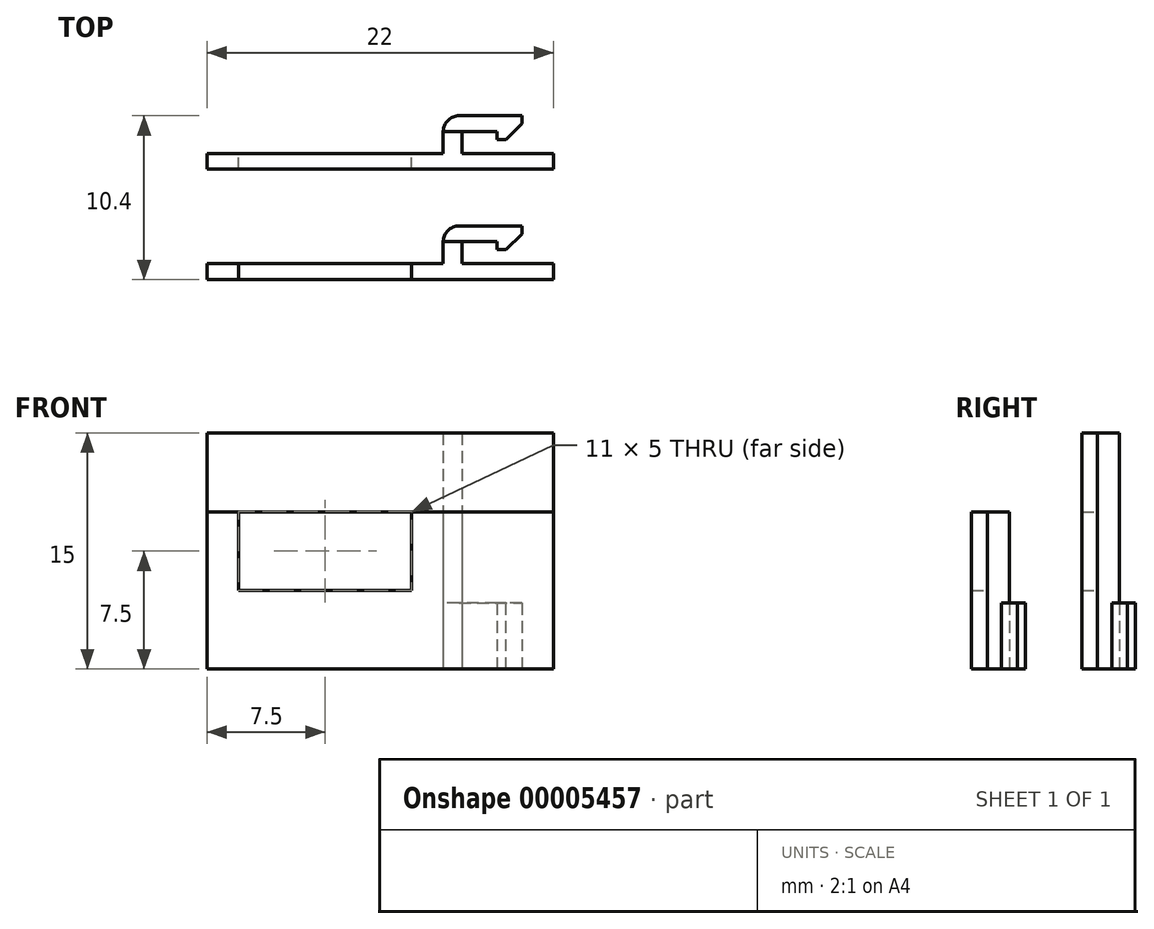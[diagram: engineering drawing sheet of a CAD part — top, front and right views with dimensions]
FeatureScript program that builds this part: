
annotation { "Feature Type Name" : "Feature", "Feature Type Description" : "" }
export const myFeature = defineFeature(function(context is Context, id is Id, definition is map)
    precondition{}
    {
        {
            var Q0;
            Q0=qCreatedBy(makeId("Top.planeOp"),FACE);
            var sketch = newSketch(context, id + "F0", { "sketchPlane" : qUnion([Q0])});
            skLineSegment(sketch, "E0.bottom", {"start": v(7, 0) * mm, "end": v(-15, 0) * mm});
            skLineSegment(sketch, "E0.top", {"start": v(7, -1) * mm, "end": v(-15, -1) * mm});
            skLineSegment(sketch, "E0.left", {"start": v(7, 0) * mm, "end": v(7, -1) * mm});
            skLineSegment(sketch, "E0.right", {"start": v(-15, 0) * mm, "end": v(-15, -1) * mm});
            skLineSegment(sketch, "E1", {"start": v(0, 0) * mm, "end": v(0, 1.4) * mm});
            skLineSegment(sketch, "E2", {"start": v(1, 2.4) * mm, "end": v(5, 2.4) * mm});
            skLineSegment(sketch, "E3", {"start": v(5, 2.4) * mm, "end": v(5, 0.9) * mm});
            skLineSegment(sketch, "E4", {"start": v(5, 0.9) * mm, "end": v(3.4, 0.9) * mm});
            skLineSegment(sketch, "E5", {"start": v(3.4, 0.9) * mm, "end": v(3.4, 1.4) * mm});
            skLineSegment(sketch, "E6", {"start": v(3.4, 1.4) * mm, "end": v(1.2, 1.4) * mm});
            skLineSegment(sketch, "E7", {"start": v(1.2, 1.4) * mm, "end": v(1.2, 0) * mm});
            skPoint(sketch, "E8.visualSharp", {"position": v(3.4, 0.9) * mm});
            skPoint(sketch, "E9.visualSharp", {"position": v(5, 0.9) * mm});
            skPoint(sketch, "E10.visualSharp", {"position": v(5, 2.4) * mm});
            skPoint(sketch, "E11.visualSharp", {"position": v(0, 2.4) * mm});
            skArc(sketch, "E11.filletArc", {"start": v(1, 2.4) * mm, "mid": v(0.3, 2.1) * mm, "end": v(0, 1.4) * mm});
            skLineSegment(sketch, "E12", {"start": v(0, 1.4) * mm, "end": v(1.2, 1.4) * mm});
            skSolve(sketch);
        }
        {
            var Q0;
            Q0=makeQuery(id+"F0.imprint","IMPRINT",FACE,{"disambiguationData":[TD([[makeQuery(id+"F0.imprint","IMPRINT",EDGE,{"derivedFrom":sQuery(id+"F0.wireOp",EDGE,"E2")}),-1.0]])]});
            extrude(context, id + "F1", {"entities" : qUnion([Q0]), "depth" : 4.2 * mm});
        }
        {
            var Q0;
            Q0=makeQuery(id+"F0.imprint","IMPRINT",FACE,{"disambiguationData":[TD([[makeQuery(id+"F0.imprint","IMPRINT",EDGE,{"derivedFrom":sQuery(id+"F0.wireOp",EDGE,"E0.top")}),-1.0]])]});
            var Q1;
            {var subQ1=sQuery(id+"F0.wireOp",EDGE,"E1");Q1=makeQuery(id+"F0.imprint","IMPRINT",FACE,{"disambiguationData":[TD([[makeQuery(id+"F0.imprint","IMPRINT",EDGE,{"derivedFrom":subQ1}),-1.0]])]});}
            extrude(context, id + "F2", {"entities" : qUnion([Q0, Q1]), "operationType" : NewBodyOperationType.ADD, "depth" : 10 * mm});
        }
        {
            var Q0;
            Q0=makeQuery(id+"F1.opExtrude","SWEPT_BODY",BODY,{"disambiguationData":[OSD([sQuery(id+"F0.wireOp",EDGE,"E2"),sQuery(id+"F0.wireOp",EDGE,"E3"),sQuery(id+"F0.wireOp",EDGE,"E4"),sQuery(id+"F0.wireOp",EDGE,"E5"),sQuery(id+"F0.wireOp",EDGE,"E6"),sQuery(id+"F0.wireOp",EDGE,"E8.filletArc"),sQuery(id+"F0.wireOp",EDGE,"E9.filletArc"),sQuery(id+"F0.wireOp",EDGE,"E10.filletArc"),sQuery(id+"F0.wireOp",EDGE,"E11.filletArc"),sQuery(id+"F0.wireOp",EDGE,"E12")])]});
            transform(context, id + "F3", {"entities" : qUnion([Q0]), "transformType" : TransformType.TRANSLATION_3D, "dx" : 0 * mm, "dy" : 7 * mm, "dz" : 0 * mm, "makeCopy" : true});
        }
        {
            var Q0;
            Q0=makeQuery(id+"F3.opPattern","COPY",FACE,{"derivedFrom":makeQuery(id+"F2.opExtrude","CAP_FACE",FACE,{"disambiguationData":[OSD([sQuery(id+"F0.wireOp",EDGE,"E0.bottom"),sQuery(id+"F0.wireOp",EDGE,"E0.top"),sQuery(id+"F0.wireOp",EDGE,"E0.left"),sQuery(id+"F0.wireOp",EDGE,"E0.right"),sQuery(id+"F0.wireOp",EDGE,"E1"),sQuery(id+"F0.wireOp",EDGE,"E7"),sQuery(id+"F0.wireOp",EDGE,"E12")])],"isStart":false}),"instanceName":"1"});
            extrude(context, id + "F4", {"entities" : qUnion([Q0]), "operationType" : NewBodyOperationType.ADD, "offsetDistance" : 25 * mm, "depth" : 5 * mm});
        }
        {
            var Q0;
            Q0=makeQuery(id+"F1.opExtrude","SWEPT_EDGE",EDGE,{"disambiguationData":[OSD([sQuery(id+"F0.wireOp",EDGE,"E3"),sQuery(id+"F0.wireOp",EDGE,"E4")])]});
            var Q1;
            Q1=makeQuery(id+"F3.opPattern","COPY",EDGE,{"derivedFrom":makeQuery(id+"F1.opExtrude","SWEPT_EDGE",EDGE,{"disambiguationData":[OSD([sQuery(id+"F0.wireOp",EDGE,"E3"),sQuery(id+"F0.wireOp",EDGE,"E4")])]}),"instanceName":"1"});
            chamfer(context, id + "F5", {"entities" : qUnion([Q0, Q1]), "width" : 1 * mm, "tangentPropagation" : true});
        }
        {
            var Q0;
            {var subQ0=sQuery(id+"F0.wireOp",EDGE,"E0.bottom");var subQ1=makeQuery(id+"F0.imprint","IMPRINT",EDGE,{"disambiguationData":[TD([[makeQuery(id+"F0.imprint","INTERSECT",VERTEX,{"derivedFrom":[subQ0,sQuery(id+"F0.wireOp",EDGE,"E0.right")]}),1.0]])],"derivedFrom":subQ0});Q0=makeQuery(id+"F4.boolean.opBoolean","MERGE",FACE,{"derivedFrom":[makeQuery(id+"F3.opPattern","COPY",FACE,{"derivedFrom":makeQuery(id+"F2.opExtrude","SWEPT_FACE",FACE,{"disambiguationData":[OSD([subQ0]),TDD([subQ1])]}),"instanceName":"1"}),makeQuery(id+"F4.opExtrude","SWEPT_FACE",FACE,{"disambiguationData":[OSD([subQ0]),TDD([makeQuery(id+"F3.opPattern","COPY",EDGE,{"derivedFrom":makeQuery(id+"F2.opExtrude","CAP_EDGE",EDGE,{"disambiguationData":[OSD([subQ0]),TDD([subQ1])],"isStart":false}),"instanceName":"1"})])]})]});}
            var sketch = newSketch(context, id + "F6", { "sketchPlane" : qUnion([Q0])});
            skLineSegment(sketch, "E13.bottom", {"start": v(13, 5) * mm, "end": v(2, 5) * mm});
            skLineSegment(sketch, "E13.top", {"start": v(13, 10) * mm, "end": v(2, 10) * mm});
            skLineSegment(sketch, "E13.left", {"start": v(13, 5) * mm, "end": v(13, 10) * mm});
            skLineSegment(sketch, "E13.right", {"start": v(2, 5) * mm, "end": v(2, 10) * mm});
            skPoint(sketch, "E13.middle", {"position": v(7.5, 7.5) * mm});
            skPoint(sketch, "E13.middle.positionSnap0", {"position": v(7.5, 15) * mm});
            skPoint(sketch, "E13.middle.positionSnap1", {"position": v(15, 7.5) * mm});
            skPoint(sketch, "E13.centerSnap0", {"position": v(7.5, 15) * mm});
            skPoint(sketch, "E13.centerSnap1", {"position": v(15, 7.5) * mm});
            skSolve(sketch);
        }
        {
            var Q0;
            Q0 = qSketchRegion(id + "F6", true);
            extrude(context, id + "F7", {"entities" : qUnion([Q0]), "operationType" : NewBodyOperationType.REMOVE, "endBound" : BoundingType.THROUGH_ALL, "oppositeDirection" : true, "depth" : 25 * mm, "offsetDistance" : 25 * mm});
        }
    });
